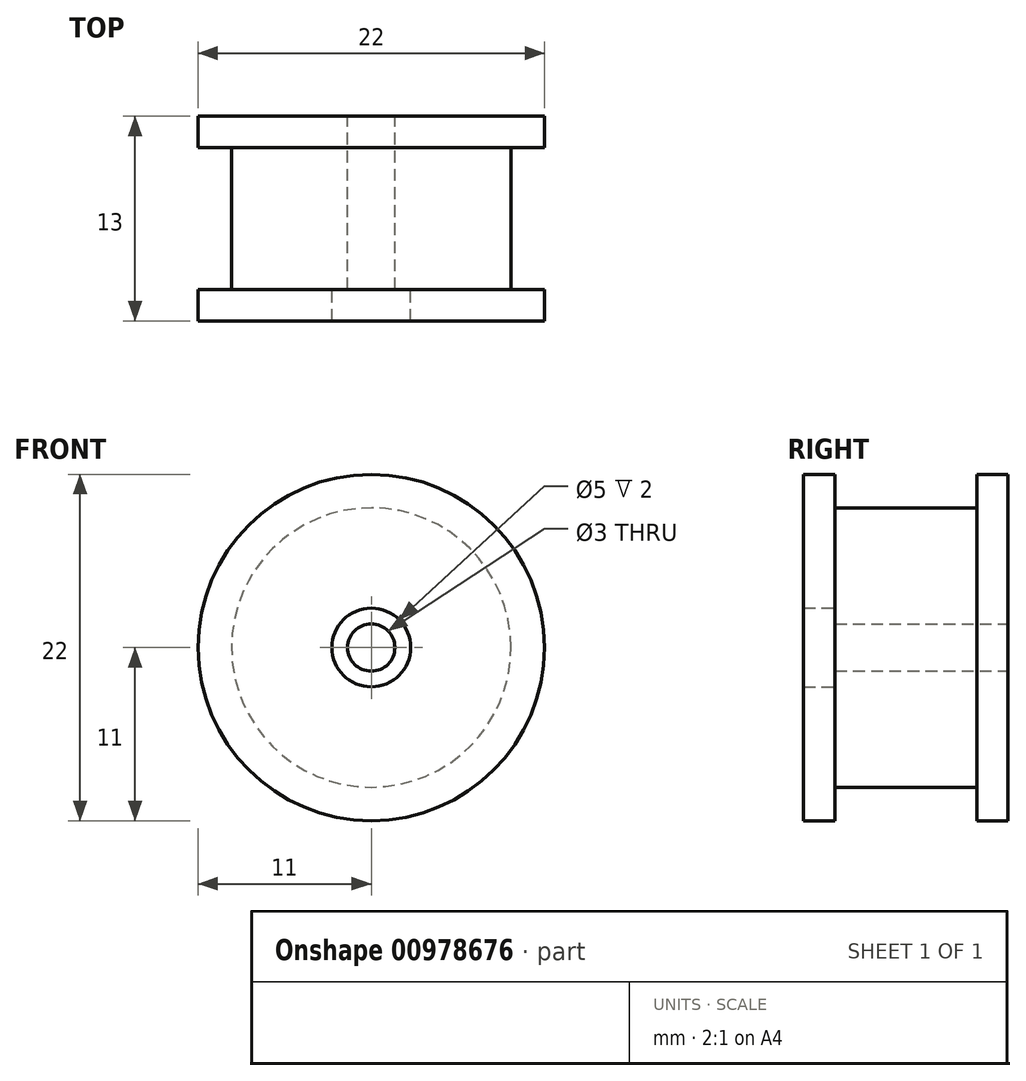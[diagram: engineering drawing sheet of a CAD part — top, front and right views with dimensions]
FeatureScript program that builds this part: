
annotation { "Feature Type Name" : "Feature", "Feature Type Description" : "" }
export const myFeature = defineFeature(function(context is Context, id is Id, definition is map)
    precondition{}
    {
        {
            var Q0;
            Q0=qCreatedBy(makeId("Front.planeOp"),FACE);
            var sketch = newSketch(context, id + "F0", { "sketchPlane" : qUnion([Q0])});
            skCircle(sketch, "E0", {"center": v(0, 0) * mm, "radius": 11 * mm});
            skCircle(sketch, "E1", {"center": v(0, 0) * mm, "radius": 2.5 * mm});
            skSolve(sketch);
        }
        {
            var Q0;
            Q0=makeQuery(id+"F0.imprint","IMPRINT",FACE,{"disambiguationData":[TD([[makeQuery(id+"F0.imprint","IMPRINT",EDGE,{"derivedFrom":sQuery(id+"F0.wireOp",EDGE,"E0")}),1.0]])]});
            extrude(context, id + "F1", {"entities" : qUnion([Q0]), "depth" : 2 * mm, "offsetDistance" : 25 * mm});
        }
        {
            var Q0;
            Q0=makeQuery(id+"F1.opExtrude","CAP_FACE",FACE,{"disambiguationData":[OSD([sQuery(id+"F0.wireOp",EDGE,"E0"),sQuery(id+"F0.wireOp",EDGE,"E1")])],"isStart":false});
            var sketch = newSketch(context, id + "F2", { "sketchPlane" : qUnion([Q0])});
            skCircle(sketch, "E2", {"center": v(0, 0) * mm, "radius": 8.88 * mm});
            skSolve(sketch);
        }
        {
            var Q0;
            Q0=makeQuery(id+"F2.imprint","IMPRINT",FACE,{"disambiguationData":[TD([[makeQuery(id+"F2.imprint","IMPRINT",EDGE,{"derivedFrom":sQuery(id+"F2.wireOp",EDGE,"E2")}),1.0]])]});
            extrude(context, id + "F3", {"entities" : qUnion([Q0]), "operationType" : NewBodyOperationType.ADD, "depth" : 9 * mm, "offsetDistance" : 25 * mm});
        }
        {
            var Q0;
            Q0=makeQuery(id+"F3.opExtrude","CAP_FACE",FACE,{"disambiguationData":[OSD([sQuery(id+"F0.wireOp",EDGE,"E1"),sQuery(id+"F2.wireOp",EDGE,"E2")])],"isStart":false});
            var sketch = newSketch(context, id + "F4", { "sketchPlane" : qUnion([Q0])});
            skCircle(sketch, "E3.0", {"center": v(0, 0) * mm, "radius": 11 * mm});
            skSolve(sketch);
        }
        {
            var Q0;
            Q0=makeQuery(id+"F4.imprint","IMPRINT",FACE,{"disambiguationData":[TD([[makeQuery(id+"F4.imprint","IMPRINT",EDGE,{"derivedFrom":sQuery(id+"F4.wireOp",EDGE,"E3.0")}),1.0]])]});
            var Q1;
            Q1=makeQuery(id+"F4.imprint","IMPRINT",FACE,{"disambiguationData":[TD([[makeQuery(id+"F4.imprint","IMPRINT",EDGE,{"derivedFrom":makeQuery(id+"F3.opExtrude","CAP_EDGE",EDGE,{"disambiguationData":[OSD([sQuery(id+"F2.wireOp",EDGE,"E2")])],"isStart":false})}),1.0]])]});
            extrude(context, id + "F5", {"entities" : qUnion([Q0, Q1]), "operationType" : NewBodyOperationType.ADD, "depth" : 2 * mm, "offsetDistance" : 25 * mm});
        }
        {
            var Q0;
            Q0=qCreatedBy(makeId("Front.planeOp"),FACE);
            var sketch = newSketch(context, id + "F6", { "sketchPlane" : qUnion([Q0])});
            skCircle(sketch, "E4", {"center": v(0, 0) * mm, "radius": 1.5 * mm});
            skCircle(sketch, "E5", {"center": v(0, 0) * mm, "radius": 6.5 * mm});
            skSolve(sketch);
        }
        {
            var Q0;
            Q0=makeQuery(id+"F6.imprint","IMPRINT",FACE,{"disambiguationData":[TD([[makeQuery(id+"F6.imprint","IMPRINT",EDGE,{"derivedFrom":sQuery(id+"F6.wireOp",EDGE,"E4")}),-1.0]])]});
            extrude(context, id + "F7", {"entities" : qUnion([Q0]), "depth" : 2 * mm, "offsetDistance" : 25 * mm});
        }
        {
            var Q0;
            Q0=makeQuery(id+"F7.opExtrude","CAP_FACE",FACE,{"disambiguationData":[OSD([sQuery(id+"F6.wireOp",EDGE,"E4"),sQuery(id+"F6.wireOp",EDGE,"E5")])],"isStart":false});
            var sketch = newSketch(context, id + "F8", { "sketchPlane" : qUnion([Q0])});
            skCircle(sketch, "E6", {"center": v(0, 0) * mm, "radius": 4.5 * mm});
            skSolve(sketch);
        }
        {
            var Q0;
            Q0=makeQuery(id+"F8.imprint","IMPRINT",FACE,{"disambiguationData":[TD([[makeQuery(id+"F8.imprint","IMPRINT",EDGE,{"derivedFrom":sQuery(id+"F8.wireOp",EDGE,"E6")}),1.0]])]});
            extrude(context, id + "F9", {"entities" : qUnion([Q0]), "operationType" : NewBodyOperationType.ADD, "depth" : 9 * mm, "offsetDistance" : 25 * mm});
        }
        {
            var Q0;
            Q0=makeQuery(id+"F9.opExtrude","CAP_FACE",FACE,{"disambiguationData":[OSD([sQuery(id+"F6.wireOp",EDGE,"E4"),sQuery(id+"F8.wireOp",EDGE,"E6")])],"isStart":false});
            var sketch = newSketch(context, id + "F10", { "sketchPlane" : qUnion([Q0])});
            skCircle(sketch, "E7.0", {"center": v(0, 0) * mm, "radius": 6.5 * mm});
            skSolve(sketch);
        }
        {
            var Q0;
            Q0=makeQuery(id+"F10.imprint","IMPRINT",FACE,{"disambiguationData":[TD([[makeQuery(id+"F10.imprint","IMPRINT",EDGE,{"derivedFrom":sQuery(id+"F10.wireOp",EDGE,"E7.0")}),1.0]])]});
            var Q1;
            Q1=makeQuery(id+"F10.imprint","IMPRINT",FACE,{"disambiguationData":[TD([[makeQuery(id+"F10.imprint","IMPRINT",EDGE,{"derivedFrom":makeQuery(id+"F9.opExtrude","CAP_EDGE",EDGE,{"disambiguationData":[OSD([sQuery(id+"F8.wireOp",EDGE,"E6")])],"isStart":false})}),1.0]])]});
            extrude(context, id + "F11", {"entities" : qUnion([Q0, Q1]), "operationType" : NewBodyOperationType.ADD, "depth" : 2 * mm, "offsetDistance" : 25 * mm});
        }
    });
